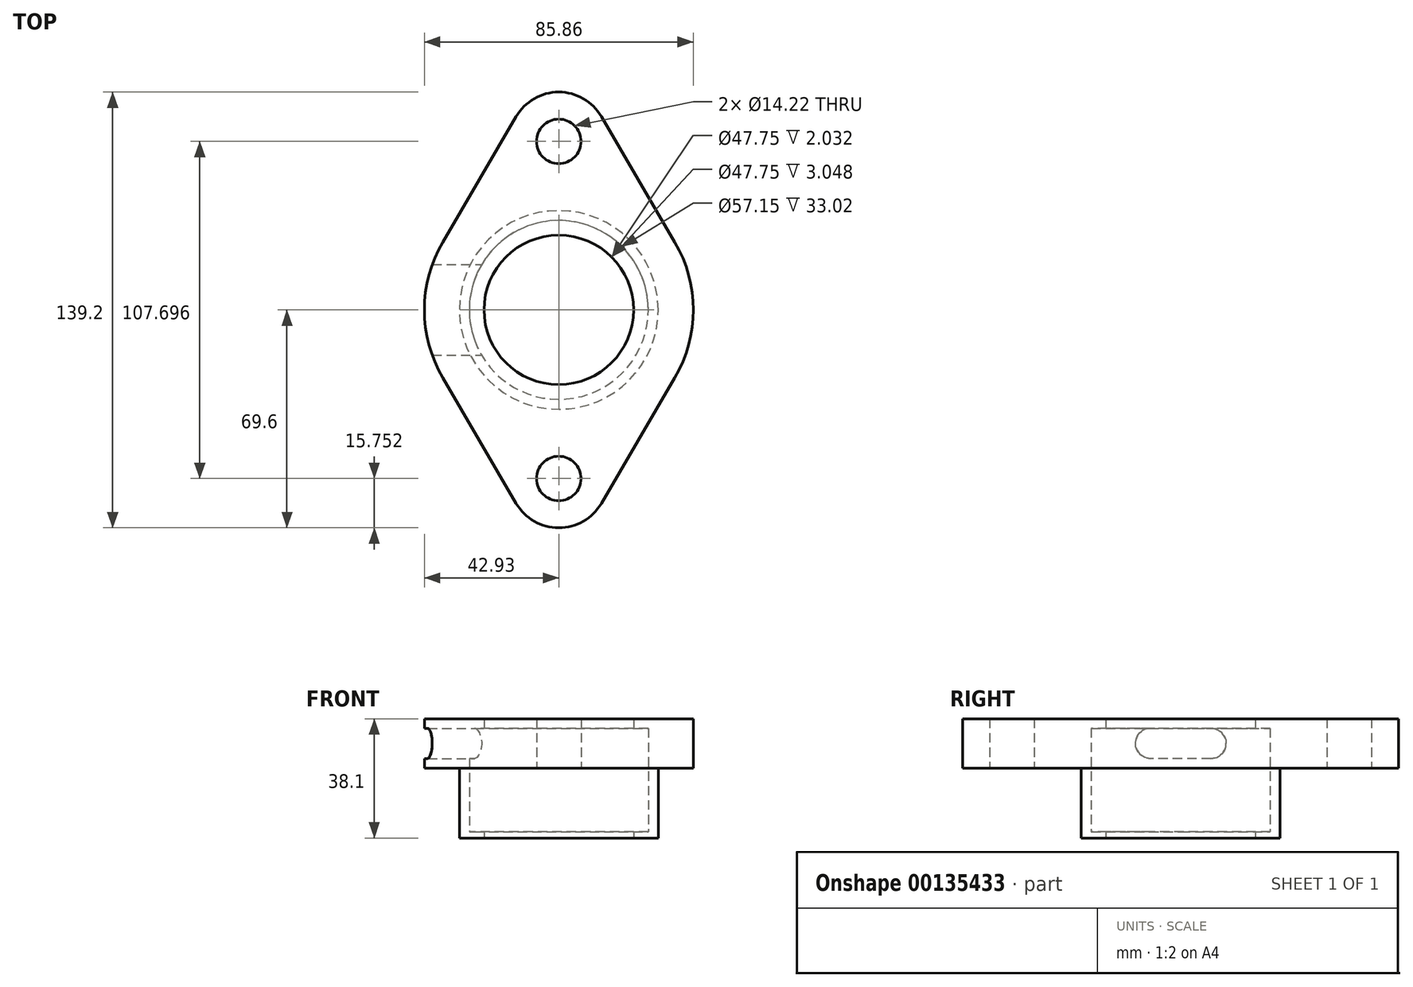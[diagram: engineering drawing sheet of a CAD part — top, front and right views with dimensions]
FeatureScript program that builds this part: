
annotation { "Feature Type Name" : "Feature", "Feature Type Description" : "" }
export const myFeature = defineFeature(function(context is Context, id is Id, definition is map)
    precondition{}
    {
        {
            var Q0;
            Q0=qCreatedBy(makeId("Top.planeOp"),FACE);
            var sketch = newSketch(context, id + "F0", { "sketchPlane" : qUnion([Q0])});
            skCircle(sketch, "E0", {"center": v(0, 0) * mm, "radius": 42.93 * mm});
            skLineSegment(sketch, "E1", {"start": v(-37.06, 21.67) * mm, "end": v(-13.6, 61.8) * mm});
            skLineSegment(sketch, "E2", {"start": v(37.06, 21.67) * mm, "end": v(13.6, 61.8) * mm});
            skLineSegment(sketch, "E3", {"start": v(-37.06, -21.67) * mm, "end": v(-13.6, -61.8) * mm});
            skLineSegment(sketch, "E4", {"start": v(37.06, -21.67) * mm, "end": v(13.6, -61.8) * mm});
            skCircle(sketch, "E5", {"center": v(0, 53.85) * mm, "radius": 7.11 * mm});
            skCircle(sketch, "E6", {"center": v(0, -53.85) * mm, "radius": 7.11 * mm});
            skArc(sketch, "E7", {"start": v(-13.6, 61.8) * mm, "mid": v(0, 69.6) * mm, "end": v(13.6, 61.8) * mm});
            skArc(sketch, "E8", {"start": v(-13.6, -61.8) * mm, "mid": v(0, -69.6) * mm, "end": v(13.6, -61.8) * mm});
            skCircle(sketch, "E9", {"center": v(0, 0) * mm, "radius": 23.88 * mm});
            skSolve(sketch);
        }
        {
            var Q0;
            Q0 = qSketchRegion(id + "F0", true);
            extrude(context, id + "F1", {"entities" : qUnion([Q0]), "depth" : 15.75 * mm});
        }
        {
            var Q0;
            Q0=qCreatedBy(makeId("Top.planeOp"),FACE);
            var sketch = newSketch(context, id + "F2", { "sketchPlane" : qUnion([Q0])});
            skCircle(sketch, "E10", {"center": v(0, 0) * mm, "radius": 23.88 * mm});
            skCircle(sketch, "E11", {"center": v(0, 0) * mm, "radius": 31.75 * mm});
            skSolve(sketch);
        }
        {
            var Q0;
            Q0 = qSketchRegion(id + "F2", true);
            extrude(context, id + "F3", {"entities" : qUnion([Q0]), "operationType" : NewBodyOperationType.ADD, "oppositeDirection" : true, "depth" : 22.35 * mm});
        }
        {
            var Q0;
            Q0=qCreatedBy(makeId("Right.planeOp"),FACE);
            var sketch = newSketch(context, id + "F4", { "sketchPlane" : qUnion([Q0])});
            skLineSegment(sketch, "E12", {"start": v(9.65, 7.87) * mm, "end": v(-9.65, 7.87) * mm, "construction": true});
            skArc(sketch, "E13.0.startCap", {"start": v(9.65, 12.7) * mm, "mid": v(14.48, 7.87) * mm, "end": v(9.65, 3.05) * mm});
            skArc(sketch, "E13.0.endCap", {"start": v(-9.65, 3.05) * mm, "mid": v(-14.48, 7.87) * mm, "end": v(-9.65, 12.7) * mm});
            skLineSegment(sketch, "E13.0.left", {"start": v(9.65, 3.05) * mm, "end": v(-9.65, 3.05) * mm});
            skLineSegment(sketch, "E13.0.right", {"start": v(9.65, 12.7) * mm, "end": v(-9.65, 12.7) * mm});
            skSolve(sketch);
        }
        {
            var Q0;
            Q0 = qSketchRegion(id + "F4", true);
            extrude(context, id + "F5", {"entities" : qUnion([Q0]), "operationType" : NewBodyOperationType.REMOVE, "endBound" : BoundingType.THROUGH_ALL, "oppositeDirection" : true, "depth" : 25.4 * mm});
        }
        {
            var Q0;
            Q0=qCreatedBy(makeId("Top.planeOp"),FACE);
            var sketch = newSketch(context, id + "F6", { "sketchPlane" : qUnion([Q0])});
            skCircle(sketch, "E14", {"center": v(0, 0) * mm, "radius": 28.58 * mm});
            skSolve(sketch);
        }
        {
            var Q0;
            Q0 = qSketchRegion(id + "F6", true);
            extrude(context, id + "F7", {"entities" : qUnion([Q0]), "operationType" : NewBodyOperationType.REMOVE, "depth" : 12.7 * mm, "hasSecondDirection" : true, "secondDirectionOppositeDirection" : true, "secondDirectionDepth" : 20.32 * mm});
        }
    });
